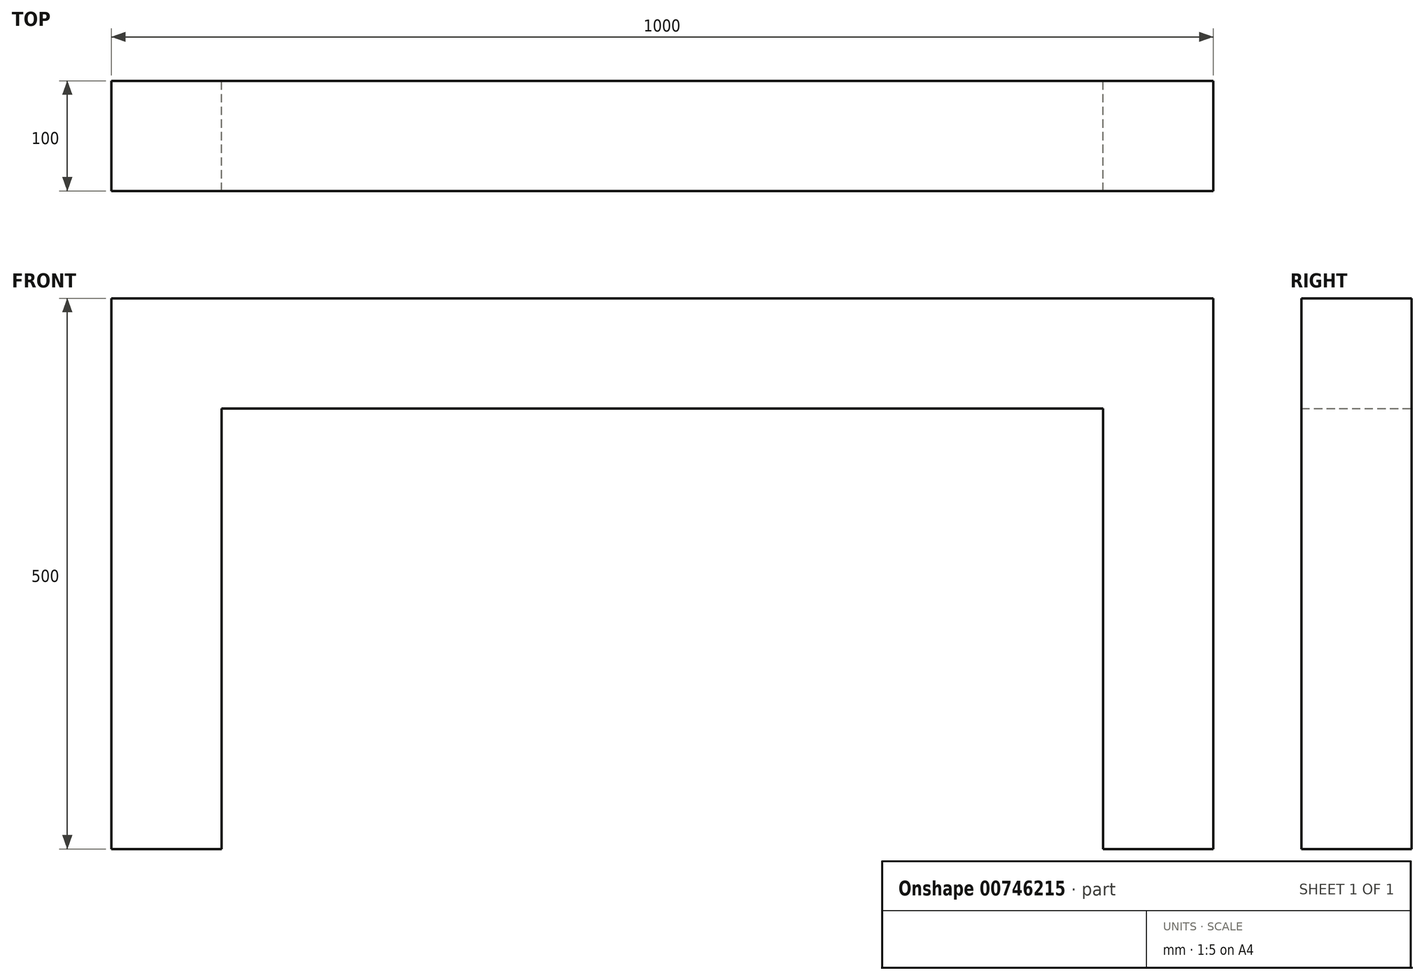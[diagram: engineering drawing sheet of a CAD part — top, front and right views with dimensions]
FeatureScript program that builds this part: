
annotation { "Feature Type Name" : "Feature", "Feature Type Description" : "" }
export const myFeature = defineFeature(function(context is Context, id is Id, definition is map)
    precondition{}
    {
        {
            var Q0;
            Q0=qCreatedBy(makeId("Front.planeOp"),FACE);
            var sketch = newSketch(context, id + "F0", { "sketchPlane" : qUnion([Q0])});
            skLineSegment(sketch, "E0", {"start": v(-500, 500) * mm, "end": v(-500, 0) * mm});
            skLineSegment(sketch, "E1", {"start": v(-500, 0) * mm, "end": v(-400, 0) * mm});
            skLineSegment(sketch, "E2", {"start": v(-400, 0) * mm, "end": v(-400, 400) * mm});
            skLineSegment(sketch, "E3", {"start": v(-400, 400) * mm, "end": v(0, 400) * mm});
            skLineSegment(sketch, "E4", {"start": v(0, 400) * mm, "end": v(0, 500) * mm});
            skLineSegment(sketch, "E5", {"start": v(0, 500) * mm, "end": v(-500, 500) * mm});
            skLineSegment(sketch, "E6", {"start": v(0, 1129.8) * mm, "end": v(0, -547.54) * mm, "construction": true});
            skLineSegment(sketch, "E7.MirrorCS", {"start": v(0, 500) * mm, "end": v(500, 500) * mm});
            skLineSegment(sketch, "E8.MirrorCS", {"start": v(400, 400) * mm, "end": v(0, 400) * mm});
            skLineSegment(sketch, "E9.MirrorCS", {"start": v(500, 500) * mm, "end": v(500, 0) * mm});
            skLineSegment(sketch, "E10.MirrorCS", {"start": v(400, 0) * mm, "end": v(400, 400) * mm});
            skLineSegment(sketch, "E11.MirrorCS", {"start": v(500, 0) * mm, "end": v(400, 0) * mm});
            skSolve(sketch);
        }
        {
            var Q0;
            Q0=makeQuery(id+"F0.imprint","IMPRINT",FACE,{"disambiguationData":[TD([[makeQuery(id+"F0.imprint","IMPRINT",EDGE,{"derivedFrom":sQuery(id+"F0.wireOp",EDGE,"E0")}),1.0]])]});
            var Q1;
            Q1=makeQuery(id+"F0.imprint","IMPRINT",FACE,{"disambiguationData":[TD([[makeQuery(id+"F0.imprint","IMPRINT",EDGE,{"derivedFrom":sQuery(id+"F0.wireOp",EDGE,"E4")}),-1.0]])]});
            extrude(context, id + "F1", {"entities" : qUnion([Q0, Q1]), "depth" : 100 * mm, "offsetDistance" : 25 * mm});
        }
    });
